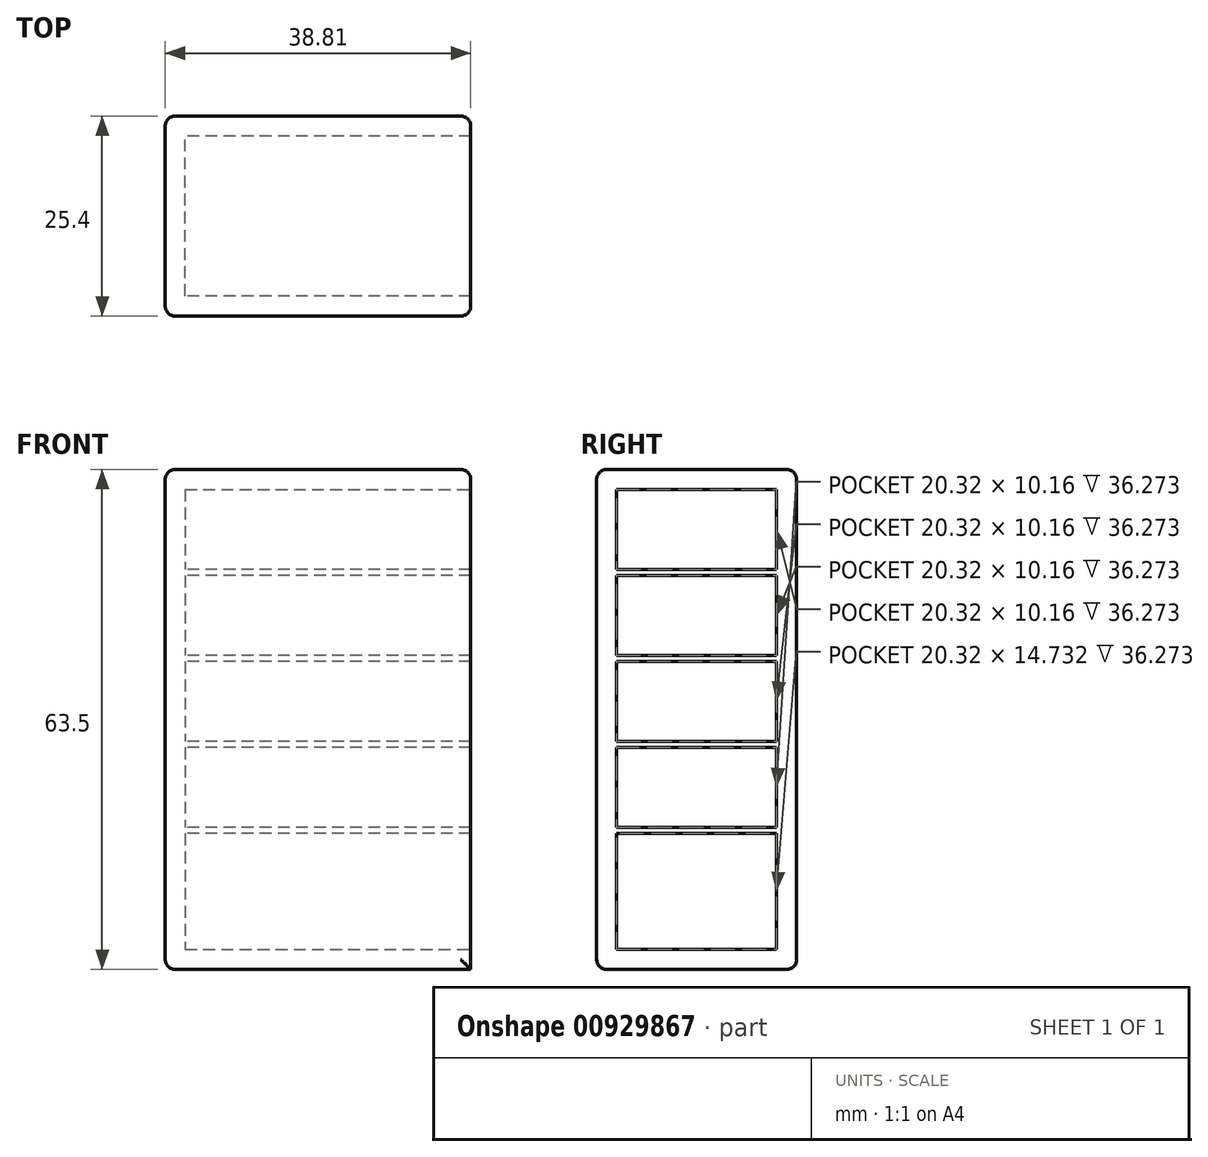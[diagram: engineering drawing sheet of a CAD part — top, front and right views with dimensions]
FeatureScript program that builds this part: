
annotation { "Feature Type Name" : "Feature", "Feature Type Description" : "" }
export const myFeature = defineFeature(function(context is Context, id is Id, definition is map)
    precondition{}
    {
        {
            var Q0;
            Q0=qCreatedBy(makeId("Front.planeOp"),FACE);
            var sketch = newSketch(context, id + "F0", { "sketchPlane" : qUnion([Q0])});
            skLineSegment(sketch, "E0.bottom", {"start": v(-49.65, 42.11) * mm, "end": v(-10.84, 42.11) * mm});
            skLineSegment(sketch, "E0.top", {"start": v(-49.65, -21.39) * mm, "end": v(-10.84, -21.39) * mm});
            skLineSegment(sketch, "E0.left", {"start": v(-49.65, 42.11) * mm, "end": v(-49.65, -21.39) * mm});
            skLineSegment(sketch, "E0.right", {"start": v(-10.84, 42.11) * mm, "end": v(-10.84, -21.39) * mm});
            skLineSegment(sketch, "E1", {"start": v(-49.65, 29.41) * mm, "end": v(-10.84, 29.41) * mm});
            skLineSegment(sketch, "E2", {"start": v(-49.65, 16.71) * mm, "end": v(-10.84, 16.71) * mm});
            skLineSegment(sketch, "E3", {"start": v(-49.65, 4.01) * mm, "end": v(-10.84, 4.01) * mm});
            skLineSegment(sketch, "E4", {"start": v(-49.65, -8.69) * mm, "end": v(-10.84, -8.69) * mm});
            skSolve(sketch);
        }
        {
            var Q0;
            {var subQ0=sQuery(id+"F0.wireOp",EDGE,"E3");Q0=makeQuery(id+"F0.imprint","IMPRINT",FACE,{"disambiguationData":[TD([[makeQuery(id+"F0.imprint","IMPRINT",EDGE,{"derivedFrom":subQ0}),-1.0]])]});}
            var Q1;
            {var subQ0=sQuery(id+"F0.wireOp",EDGE,"E0.bottom");Q1=makeQuery(id+"F0.imprint","IMPRINT",FACE,{"disambiguationData":[TD([[makeQuery(id+"F0.imprint","IMPRINT",EDGE,{"derivedFrom":subQ0}),-1.0]])]});}
            var Q2;
            {var subQ0=sQuery(id+"F0.wireOp",EDGE,"E1");Q2=makeQuery(id+"F0.imprint","IMPRINT",FACE,{"disambiguationData":[TD([[makeQuery(id+"F0.imprint","IMPRINT",EDGE,{"derivedFrom":subQ0}),-1.0]])]});}
            var Q3;
            {var subQ0=sQuery(id+"F0.wireOp",EDGE,"E2");Q3=makeQuery(id+"F0.imprint","IMPRINT",FACE,{"disambiguationData":[TD([[makeQuery(id+"F0.imprint","IMPRINT",EDGE,{"derivedFrom":subQ0}),-1.0]])]});}
            var Q4;
            {var subQ0=sQuery(id+"F0.wireOp",EDGE,"E0.top");Q4=makeQuery(id+"F0.imprint","IMPRINT",FACE,{"disambiguationData":[TD([[makeQuery(id+"F0.imprint","IMPRINT",EDGE,{"derivedFrom":subQ0}),1.0]])]});}
            extrude(context, id + "F1", {"entities" : qUnion([Q0, Q1, Q2, Q3, Q4]), "depth" : 25.4 * mm, "offsetDistance" : 25.4 * mm});
        }
        {
            var Q0;
            Q0=makeQuery(id+"F1.opExtrude","SWEPT_FACE",FACE,{"disambiguationData":[OSD([sQuery(id+"F0.wireOp",EDGE,"E0.right")])]});
            shell(context, id + "F2", {"entities" : qUnion([Q0]), "thickness" : 2.54 * mm});
        }
        {
            var Q0;
            Q0=makeQuery(id+"F2.opShell","OFFSET_FACE",FACE,{"disambiguationData":[OSD([sQuery(id+"F0.wireOp",EDGE,"E0.left")])]});
            var sketch = newSketch(context, id + "F3", { "sketchPlane" : qUnion([Q0])});
            skLineSegment(sketch, "E5.bottom", {"start": v(-22.86, 29.41) * mm, "end": v(-2.54, 29.41) * mm});
            skLineSegment(sketch, "E5.top", {"start": v(-22.86, 28.65) * mm, "end": v(-2.54, 28.65) * mm});
            skLineSegment(sketch, "E5.left", {"start": v(-22.86, 29.41) * mm, "end": v(-22.86, 28.65) * mm});
            skLineSegment(sketch, "E5.right", {"start": v(-2.54, 29.41) * mm, "end": v(-2.54, 28.65) * mm});
            skLineSegment(sketch, "E6.bottom", {"start": v(-22.86, 18.49) * mm, "end": v(-2.54, 18.49) * mm});
            skLineSegment(sketch, "E6.top", {"start": v(-22.86, 17.73) * mm, "end": v(-2.54, 17.73) * mm});
            skLineSegment(sketch, "E6.left", {"start": v(-22.86, 18.49) * mm, "end": v(-22.86, 17.73) * mm});
            skLineSegment(sketch, "E6.right", {"start": v(-2.54, 18.49) * mm, "end": v(-2.54, 17.73) * mm});
            skLineSegment(sketch, "E7.bottom", {"start": v(-22.86, 7.57) * mm, "end": v(-2.54, 7.57) * mm});
            skLineSegment(sketch, "E7.top", {"start": v(-22.86, 6.8) * mm, "end": v(-2.54, 6.8) * mm});
            skLineSegment(sketch, "E7.left", {"start": v(-22.86, 7.57) * mm, "end": v(-22.86, 6.8) * mm});
            skLineSegment(sketch, "E7.right", {"start": v(-2.54, 7.57) * mm, "end": v(-2.54, 6.8) * mm});
            skLineSegment(sketch, "E8.bottom", {"start": v(-22.86, -3.36) * mm, "end": v(-2.54, -3.36) * mm});
            skLineSegment(sketch, "E8.top", {"start": v(-22.86, -4.12) * mm, "end": v(-2.54, -4.12) * mm});
            skLineSegment(sketch, "E8.left", {"start": v(-22.86, -3.36) * mm, "end": v(-22.86, -4.12) * mm});
            skLineSegment(sketch, "E8.right", {"start": v(-2.54, -3.36) * mm, "end": v(-2.54, -4.12) * mm});
            skSolve(sketch);
        }
        {
            var Q0;
            Q0=makeQuery(id+"F3.imprint","IMPRINT",FACE,{"disambiguationData":[TD([[makeQuery(id+"F3.imprint","IMPRINT",EDGE,{"derivedFrom":sQuery(id+"F3.wireOp",EDGE,"E5.bottom")}),-1.0]])]});
            var Q1;
            Q1=makeQuery(id+"F3.imprint","IMPRINT",FACE,{"disambiguationData":[TD([[makeQuery(id+"F3.imprint","IMPRINT",EDGE,{"derivedFrom":sQuery(id+"F3.wireOp",EDGE,"E6.bottom")}),-1.0]])]});
            var Q2;
            Q2=makeQuery(id+"F3.imprint","IMPRINT",FACE,{"disambiguationData":[TD([[makeQuery(id+"F3.imprint","IMPRINT",EDGE,{"derivedFrom":sQuery(id+"F3.wireOp",EDGE,"E7.bottom")}),-1.0]])]});
            var Q3;
            Q3=makeQuery(id+"F3.imprint","IMPRINT",FACE,{"disambiguationData":[TD([[makeQuery(id+"F3.imprint","IMPRINT",EDGE,{"derivedFrom":sQuery(id+"F3.wireOp",EDGE,"E8.bottom")}),-1.0]])]});
            var Q4;
            Q4=makeQuery(id+"F1.opExtrude","SWEPT_FACE",FACE,{"disambiguationData":[OSD([sQuery(id+"F0.wireOp",EDGE,"E0.right")])]});
            extrude(context, id + "F4", {"entities" : qUnion([Q0, Q1, Q2, Q3]), "operationType" : NewBodyOperationType.ADD, "endBound" : BoundingType.UP_TO_SURFACE, "depth" : 25.4 * mm, "endBoundEntityFace" : qUnion([Q4]), "offsetDistance" : 25.4 * mm});
        }
        {
            var Q0;
            Q0=makeQuery(id+"F1.opExtrude","CAP_FACE",FACE,{"disambiguationData":[OSD([sQuery(id+"F0.wireOp",EDGE,"E0.bottom"),sQuery(id+"F0.wireOp",EDGE,"E0.top"),sQuery(id+"F0.wireOp",EDGE,"E0.left"),sQuery(id+"F0.wireOp",EDGE,"E0.right")])],"isStart":false});
            var Q1;
            Q1=makeQuery(id+"F1.opExtrude","SWEPT_FACE",FACE,{"disambiguationData":[OSD([sQuery(id+"F0.wireOp",EDGE,"E0.left")])]});
            var Q2;
            Q2=makeQuery(id+"F1.opExtrude","CAP_EDGE",EDGE,{"disambiguationData":[OSD([sQuery(id+"F0.wireOp",EDGE,"E0.right")])],"isStart":true});
            var Q3;
            Q3=makeQuery(id+"F1.opExtrude","CAP_EDGE",EDGE,{"disambiguationData":[OSD([sQuery(id+"F0.wireOp",EDGE,"E0.bottom")])],"isStart":true});
            var Q4;
            Q4=makeQuery(id+"F1.opExtrude","CAP_EDGE",EDGE,{"disambiguationData":[OSD([sQuery(id+"F0.wireOp",EDGE,"E0.top")])],"isStart":true});
            var Q5;
            Q5=makeQuery(id+"F1.opExtrude","SWEPT_EDGE",EDGE,{"disambiguationData":[OSD([sQuery(id+"F0.wireOp",EDGE,"E0.bottom"),sQuery(id+"F0.wireOp",EDGE,"E0.right")])]});
            fillet(context, id + "F5", {"entities" : qUnion([Q0, Q1, Q2, Q3, Q4, Q5]), "radius" : 1.27 * mm, "tangentPropagation" : true, "allowEdgeOverflow" : false});
        }
    });
